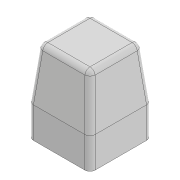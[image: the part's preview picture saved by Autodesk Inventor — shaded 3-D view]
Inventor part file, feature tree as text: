
AUTODESK INVENTOR PART (.ipt)
format: ipt  version: 2020 (Build 240168000, 168)  size: 130,048 bytes
history: native  units: mm
features: chamfer x4, extrude x2, sketch x2, other x1, fillet x1
ambient origin geometry x8: Origin, YZ Plane, XZ Plane, XY Plane, X Axis, Y Axis, Z Axis, Center Point
bodies: Body1 (feature_tree)
feature tree (10):
  other  "ソリッド1"
  extrude  "押し出し1"  Depth=60.0mm
  chamfer  "面取り1"  Distance=60.0mm
  chamfer  "面取り2"  Distance=80.0mm
  chamfer  "面取り3"  Distance=5.0mm Angle=45.0deg
  chamfer  "面取り4"  Distance=5.0mm Angle=45.0deg
  fillet  "フィレット1"  Radius=5.0mm
  extrude  "押し出し2"  Depth=5.0mm TaperAngle=45.0deg
  sketch  "スケッチ1"
  sketch  "スケッチ2"
